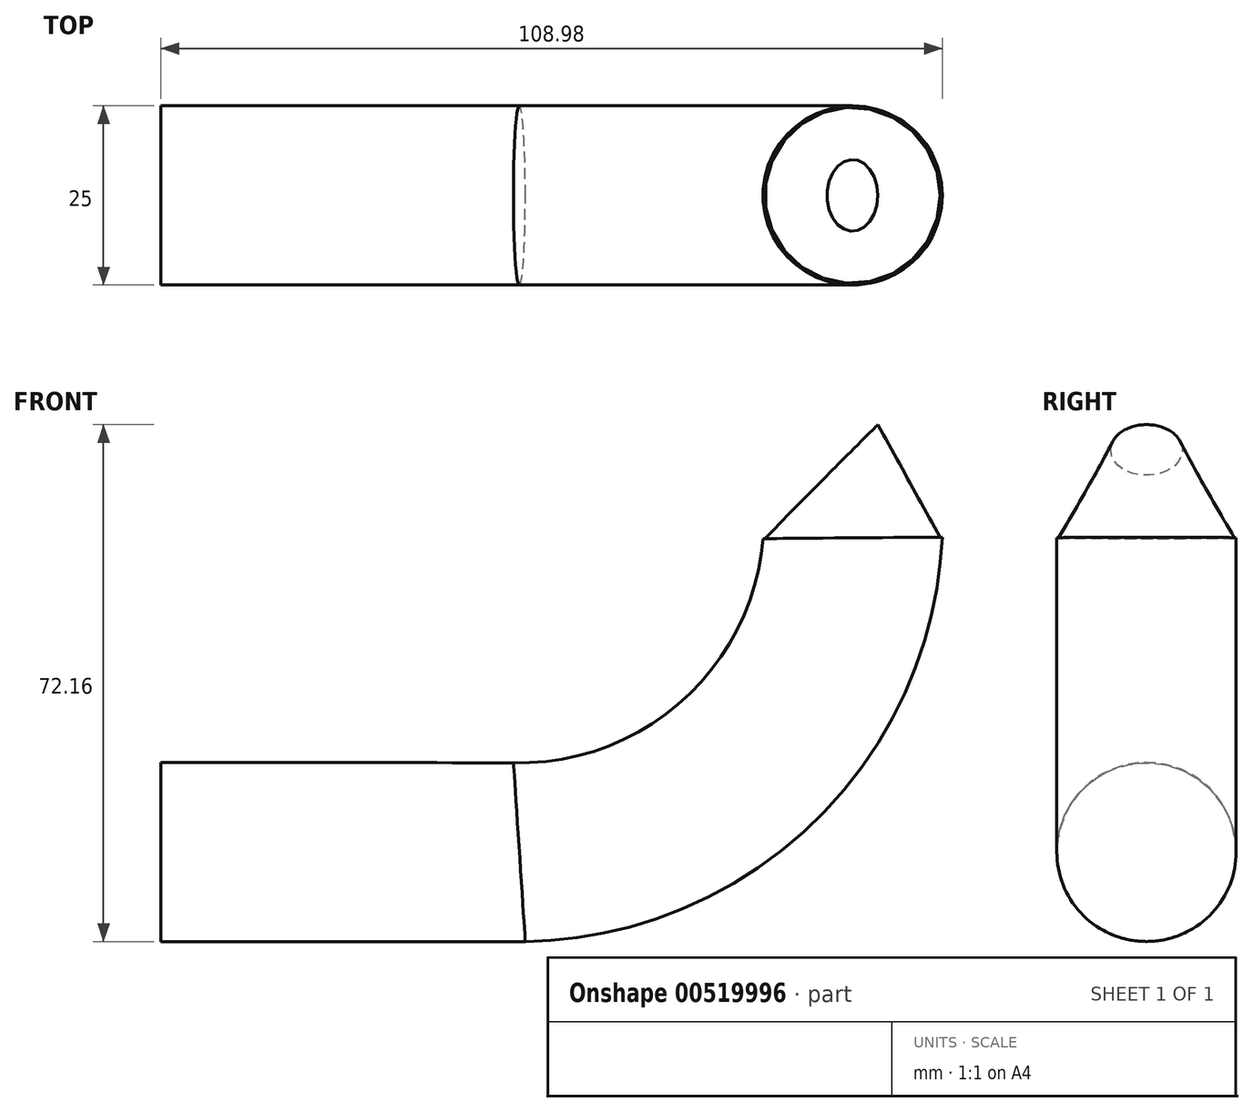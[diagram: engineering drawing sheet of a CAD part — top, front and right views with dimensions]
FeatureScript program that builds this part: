
annotation { "Feature Type Name" : "Feature", "Feature Type Description" : "" }
export const myFeature = defineFeature(function(context is Context, id is Id, definition is map)
    precondition{}
    {
        {
            var Q0;
            Q0=qCreatedBy(makeId("Front.planeOp"),FACE);
            var sketch = newSketch(context, id + "F0", { "sketchPlane" : qUnion([Q0])});
            skLineSegment(sketch, "E0", {"start": v(-96.46, 0) * mm, "end": v(-96.46, 100) * mm});
            skLineSegment(sketch, "E1", {"start": v(-96.46, 100) * mm, "end": v(3.54, 100) * mm});
            skLineSegment(sketch, "E2", {"start": v(3.54, 100) * mm, "end": v(3.54, 90) * mm});
            skLineSegment(sketch, "E3", {"start": v(3.54, 90) * mm, "end": v(-3.54, 82.93) * mm});
            skLineSegment(sketch, "E4", {"start": v(-96.46, 50) * mm, "end": v(-96.46, 30.34) * mm});
            skPoint(sketch, "E5", {"position": v(0, 86.46) * mm});
            skLineSegment(sketch, "E6", {"start": v(0, 86.46) * mm, "end": v(0, 74.2) * mm});
            skPoint(sketch, "E7", {"position": v(0, 73.81) * mm});
            skLineSegment(sketch, "E8", {"start": v(-96.46, 30.34) * mm, "end": v(-46.46, 30.34) * mm});
            skArc(sketch, "E9", {"start": v(-46.46, 30.34) * mm, "mid": v(-14.52, 43.04) * mm, "end": v(0, 74.2) * mm});
            skLineSegment(sketch, "E10", {"start": v(-96.46, 20.34) * mm, "end": v(-46.46, 20.34) * mm});
            skLineSegment(sketch, "E11", {"start": v(-96.46, 20.34) * mm, "end": v(-96.46, 50) * mm});
            skSolve(sketch);
        }
        {
            var Q0;
            Q0=sQuery(id+"F0.wireOp",VERTEX,"E7");
            var Q1;
            Q1=qCreatedBy(makeId("Top.planeOp"),FACE);
            cPlane(context, id + "F1", {"entities" : qUnion([Q0, Q1]), "cplaneType" : CPlaneType.PLANE_POINT, "offset" : 25 * mm, "width" : 150 * mm, "height" : 150 * mm});
        }
        {
            var Q0;
            Q0=qCreatedBy(id+"F1.planeOp",FACE);
            var sketch = newSketch(context, id + "F2", { "sketchPlane" : qUnion([Q0])});
            skCircle(sketch, "E12", {"center": v(0, 0) * mm, "radius": 12.5 * mm});
            skSolve(sketch);
        }
        {
            var Q0;
            Q0=sQuery(id+"F0.wireOp",EDGE,"E3");
            cPlane(context, id + "F3", {"entities" : qUnion([Q0]), "cplaneType" : CPlaneType.LINE_ANGLE, "offset" : 25 * mm, "angle" : 90 * degree, "width" : 150 * mm, "height" : 150 * mm});
        }
        {
            var Q0;
            Q0=qCreatedBy(id+"F3.planeOp",FACE);
            var sketch = newSketch(context, id + "F4", { "sketchPlane" : qUnion([Q0])});
            skCircle(sketch, "E13", {"center": v(0, 61.14) * mm, "radius": 5 * mm});
            skSolve(sketch);
        }
        {
            var Q0;
            Q0=makeQuery(id+"F4.imprint","IMPRINT",FACE,{"disambiguationData":[TD([[makeQuery(id+"F4.imprint","IMPRINT",EDGE,{"derivedFrom":sQuery(id+"F4.wireOp",EDGE,"E13")}),1.0]])]});
            var Q1;
            Q1=makeQuery(id+"F2.imprint","IMPRINT",FACE,{"disambiguationData":[TD([[makeQuery(id+"F2.imprint","IMPRINT",EDGE,{"derivedFrom":sQuery(id+"F2.wireOp",EDGE,"E12")}),1.0]])]});
            loft(context, id + "F5", {"sheetProfilesArray" : [{ "sheetProfileEntities" : qUnion([Q0]) }, { "sheetProfileEntities" : qUnion([Q1]) }]});
        }
        {
            var Q0;
            Q0=makeQuery(id+"F5.opLoft","CAP_FACE",FACE,{"disambiguationData":[OSD([makeQuery(id+"F2.imprint","IMPRINT",FACE,{"disambiguationData":[TD([[makeQuery(id+"F2.imprint","IMPRINT",EDGE,{"derivedFrom":sQuery(id+"F2.wireOp",EDGE,"E12")}),1.0]])]})])],"isStart":true});
            var Q1;
            Q1=sQuery(id+"F0.wireOp",EDGE,"E9");
            sweep(context, id + "F6", {"operationType" : NewBodyOperationType.ADD, "profiles" : qUnion([Q0]), "path" : qUnion([Q1])});
        }
        {
            var Q0;
            Q0=sQuery(id+"F0.wireOp",EDGE,"E11");
            cPlane(context, id + "F7", {"entities" : qUnion([Q0]), "cplaneType" : CPlaneType.LINE_ANGLE, "offset" : 25 * mm, "angle" : 0 * degree, "width" : 150 * mm, "height" : 150 * mm});
        }
        {
            var Q0;
            Q0=qCreatedBy(id+"F7.planeOp",FACE);
            var sketch = newSketch(context, id + "F8", { "sketchPlane" : qUnion([Q0])});
            skCircle(sketch, "E14", {"center": v(0, 30.34) * mm, "radius": 12.5 * mm});
            skSolve(sketch);
        }
        {
            var Q1;
            Q1=makeQuery(id+"F6.opSweep","CAP_FACE",FACE,{"disambiguationData":[OSD([sQuery(id+"F0.wireOp",VERTEX,"E9.start"),makeQuery(id+"F2.imprint","IMPRINT",FACE,{"disambiguationData":[TD([[makeQuery(id+"F2.imprint","IMPRINT",EDGE,{"derivedFrom":sQuery(id+"F2.wireOp",EDGE,"E12")}),1.0]])]})])],"isStart":false});
            var Q2;
            Q2=makeQuery(id+"F8.imprint","IMPRINT",FACE,{"disambiguationData":[TD([[makeQuery(id+"F8.imprint","IMPRINT",EDGE,{"derivedFrom":sQuery(id+"F8.wireOp",EDGE,"E14")}),1.0]])]});
            loft(context, id + "F9", {"operationType" : NewBodyOperationType.ADD, "sheetProfilesArray" : [{ "sheetProfileEntities" : qUnion([Q1]) }, { "sheetProfileEntities" : qUnion([Q2]) }]});
        }
    });
